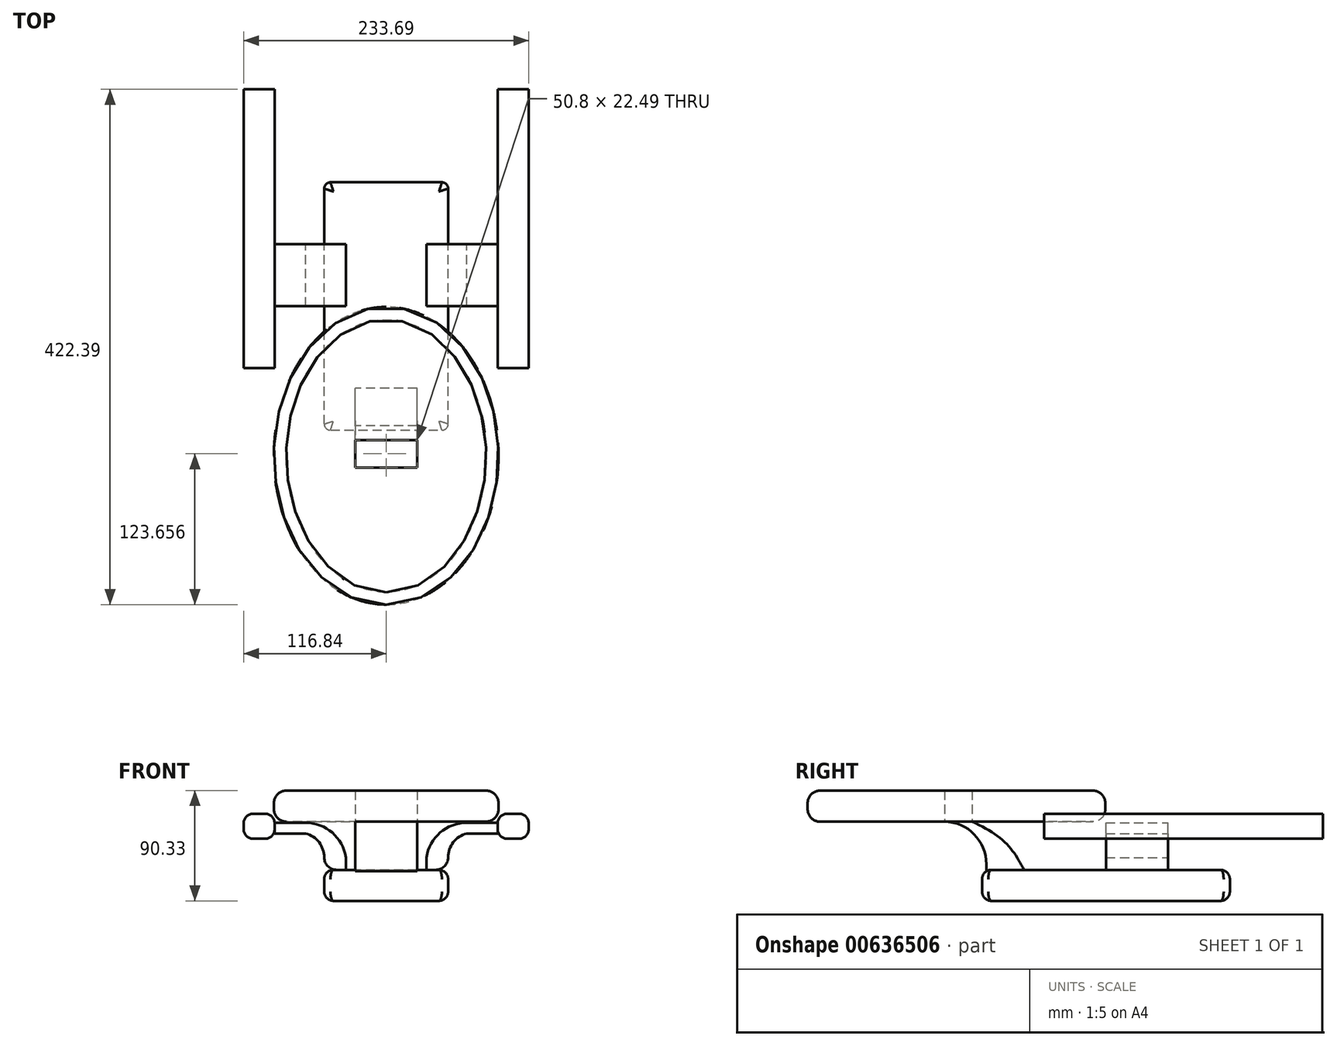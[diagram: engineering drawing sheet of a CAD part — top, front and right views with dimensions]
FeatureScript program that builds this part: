
annotation { "Feature Type Name" : "Feature", "Feature Type Description" : "" }
export const myFeature = defineFeature(function(context is Context, id is Id, definition is map)
    precondition{}
    {
        {
            var Q0;
            Q0=qCreatedBy(makeId("Front.planeOp"),FACE);
            var sketch = newSketch(context, id + "F0", { "sketchPlane" : qUnion([Q0])});
            skLineSegment(sketch, "E0.bottom", {"start": v(-50.8, 12.7) * mm, "end": v(50.8, 12.7) * mm});
            skLineSegment(sketch, "E0.top", {"start": v(-50.8, -12.7) * mm, "end": v(50.8, -12.7) * mm});
            skLineSegment(sketch, "E0.left", {"start": v(-50.8, 12.7) * mm, "end": v(-50.8, -12.7) * mm});
            skLineSegment(sketch, "E0.right", {"start": v(50.8, 12.7) * mm, "end": v(50.8, -12.7) * mm});
            skPoint(sketch, "E0.middle", {"position": v(0, 0) * mm});
            skLineSegment(sketch, "E1.bottom", {"start": v(-91.44, 38.28) * mm, "end": v(-116.84, 38.28) * mm});
            skLineSegment(sketch, "E1.top", {"start": v(-91.44, 58.6) * mm, "end": v(-116.84, 58.6) * mm});
            skLineSegment(sketch, "E1.left", {"start": v(-91.44, 38.28) * mm, "end": v(-91.44, 58.6) * mm});
            skLineSegment(sketch, "E1.right", {"start": v(-116.84, 38.28) * mm, "end": v(-116.84, 58.6) * mm});
            skPoint(sketch, "E1.middle", {"position": v(-104.14, 48.44) * mm});
            skLineSegment(sketch, "E2.bottom", {"start": v(91.45, 38.28) * mm, "end": v(116.85, 38.28) * mm});
            skLineSegment(sketch, "E2.top", {"start": v(91.45, 58.6) * mm, "end": v(116.85, 58.6) * mm});
            skLineSegment(sketch, "E2.left", {"start": v(91.45, 38.28) * mm, "end": v(91.45, 58.6) * mm});
            skLineSegment(sketch, "E2.right", {"start": v(116.85, 38.28) * mm, "end": v(116.85, 58.6) * mm});
            skPoint(sketch, "E2.middle", {"position": v(104.15, 48.44) * mm});
            skPoint(sketch, "E2.middle.positionSnap0", {"position": v(-91.44, 48.44) * mm});
            skPoint(sketch, "E2.centerSnap0", {"position": v(-91.44, 48.44) * mm});
            skLineSegment(sketch, "E3", {"start": v(50.8, 12.7) * mm, "end": v(50.8, 22.86) * mm});
            skLineSegment(sketch, "E4", {"start": v(-50.8, 12.7) * mm, "end": v(-50.8, 22.86) * mm});
            skArc(sketch, "E5", {"start": v(50.8, 22.86) * mm, "mid": v(55.06, 35.3) * mm, "end": v(66.05, 42.5) * mm});
            skLineSegment(sketch, "E6", {"start": v(66.05, 42.5) * mm, "end": v(91.45, 42.5) * mm});
            skArc(sketch, "E7", {"start": v(-50.8, 22.86) * mm, "mid": v(-55.06, 35.29) * mm, "end": v(-66.04, 42.5) * mm});
            skLineSegment(sketch, "E8", {"start": v(-66.04, 42.5) * mm, "end": v(-91.44, 42.38) * mm});
            skLineSegment(sketch, "E9", {"start": v(91.45, 51.35) * mm, "end": v(66.05, 51.35) * mm});
            skArc(sketch, "E10", {"start": v(66.05, 51.35) * mm, "mid": v(44.24, 43.24) * mm, "end": v(33.02, 22.86) * mm});
            skLineSegment(sketch, "E11", {"start": v(33.02, 22.86) * mm, "end": v(33.02, 12.7) * mm});
            skLineSegment(sketch, "E12", {"start": v(-91.44, 51.35) * mm, "end": v(-66.04, 51.35) * mm});
            skArc(sketch, "E13", {"start": v(-66.04, 51.35) * mm, "mid": v(-44.23, 43.24) * mm, "end": v(-33.02, 22.86) * mm});
            skLineSegment(sketch, "E14", {"start": v(-33.02, 22.86) * mm, "end": v(-33.02, 12.7) * mm});
            skSolve(sketch);
        }
        {
            var Q0;
            Q0=makeQuery(id+"F0.imprint","IMPRINT",FACE,{"disambiguationData":[TD([[makeQuery(id+"F0.imprint","IMPRINT",EDGE,{"derivedFrom":sQuery(id+"F0.wireOp",EDGE,"E0.top")}),1.0]])]});
            extrude(context, id + "F1", {"entities" : qUnion([Q0]), "depth" : 127 * mm, "offsetDistance" : 25.4 * mm, "hasSecondDirection" : true, "secondDirectionOppositeDirection" : true, "secondDirectionDepth" : 76.2 * mm});
        }
        {
            var Q0;
            {var subQ3=sQuery(id+"F0.wireOp",EDGE,"E2.bottom");Q0=makeQuery(id+"F0.imprint","IMPRINT",FACE,{"disambiguationData":[TD([[makeQuery(id+"F0.imprint","IMPRINT",EDGE,{"derivedFrom":subQ3}),1.0]])]});}
            extrude(context, id + "F2", {"entities" : qUnion([Q0]), "depth" : 76.2 * mm, "offsetDistance" : 25.4 * mm, "hasSecondDirection" : true, "secondDirectionOppositeDirection" : true, "secondDirectionDepth" : 152.4 * mm});
        }
        {
            var Q0;
            {var subQ3=sQuery(id+"F0.wireOp",EDGE,"E1.bottom");Q0=makeQuery(id+"F0.imprint","IMPRINT",FACE,{"disambiguationData":[TD([[makeQuery(id+"F0.imprint","IMPRINT",EDGE,{"derivedFrom":subQ3}),-1.0]])]});}
            extrude(context, id + "F3", {"entities" : qUnion([Q0]), "depth" : 76.2 * mm, "offsetDistance" : 25.4 * mm, "hasSecondDirection" : true, "secondDirectionOppositeDirection" : true, "secondDirectionDepth" : 152.4 * mm});
        }
        {
            var Q0;
            {var subQ0=sQuery(id+"F0.wireOp",EDGE,"E4");Q0=makeQuery(id+"F0.imprint","IMPRINT",FACE,{"disambiguationData":[TD([[makeQuery(id+"F0.imprint","IMPRINT",EDGE,{"derivedFrom":subQ0}),-1.0]])]});}
            extrude(context, id + "F4", {"entities" : qUnion([Q0]), "depth" : 25.4 * mm, "offsetDistance" : 25.4 * mm, "hasSecondDirection" : true, "secondDirectionOppositeDirection" : true, "secondDirectionDepth" : 25.4 * mm});
        }
        {
            var Q0;
            {var subQ0=sQuery(id+"F0.wireOp",EDGE,"E3");Q0=makeQuery(id+"F0.imprint","IMPRINT",FACE,{"disambiguationData":[TD([[makeQuery(id+"F0.imprint","IMPRINT",EDGE,{"derivedFrom":subQ0}),1.0]])]});}
            extrude(context, id + "F5", {"entities" : qUnion([Q0]), "depth" : 25.4 * mm, "offsetDistance" : 25.4 * mm, "hasSecondDirection" : true, "secondDirectionOppositeDirection" : true, "secondDirectionDepth" : 25.4 * mm});
        }
        {
            var Q0;
            Q0=qCreatedBy(makeId("Right.planeOp"),FACE);
            var sketch = newSketch(context, id + "F6", { "sketchPlane" : qUnion([Q0])});
            skLineSegment(sketch, "E15", {"start": v(-123.49, 12.39) * mm, "end": v(-123.49, 17.47) * mm});
            skArc(sketch, "E16", {"start": v(-123.49, 17.47) * mm, "mid": v(-133.92, 42.3) * mm, "end": v(-158.95, 52.23) * mm});
            skLineSegment(sketch, "E17", {"start": v(-158.95, 52.23) * mm, "end": v(-158.95, 62.4) * mm});
            skFitSpline(sketch, "E18", {"points": [v(-158.95, 62.4) * mm, v(-110.55, 37.49) * mm, v(-92.4, 12.39) * mm], "startDerivative": vector(97.08, -39.51) * mm, "endDerivative": vector(33.03, -61.53) * mm});
            skLineSegment(sketch, "E19", {"start": v(-123.49, 12.39) * mm, "end": v(-92.4, 12.39) * mm});
            skLineSegment(sketch, "E20.bottom", {"start": v(-240.74, 52.23) * mm, "end": v(-77.16, 52.23) * mm});
            skLineSegment(sketch, "E20.top", {"start": v(-240.74, 72.55) * mm, "end": v(-77.16, 72.55) * mm});
            skLineSegment(sketch, "E20.left", {"start": v(-240.74, 52.23) * mm, "end": v(-240.74, 72.55) * mm});
            skLineSegment(sketch, "E20.right", {"start": v(-77.16, 52.23) * mm, "end": v(-77.16, 72.55) * mm});
            skSolve(sketch);
        }
        {
            var Q0;
            {var subQ2=sQuery(id+"F6.wireOp",EDGE,"E15");Q0=makeQuery(id+"F6.imprint","IMPRINT",FACE,{"disambiguationData":[TD([[makeQuery(id+"F6.imprint","IMPRINT",EDGE,{"derivedFrom":subQ2}),-1.0]])]});}
            extrude(context, id + "F7", {"entities" : qUnion([Q0]), "operationType" : NewBodyOperationType.ADD, "endBound" : BoundingType.SYMMETRIC, "depth" : 50.8 * mm, "offsetDistance" : 25.4 * mm});
        }
        {
            var Q0;
            Q0=makeQuery(id+"F7.opExtrude","SWEPT_FACE",FACE,{"disambiguationData":[OSD([sQuery(id+"F6.wireOp",EDGE,"E20.bottom")])]});
            var sketch = newSketch(context, id + "F8", { "sketchPlane" : qUnion([Q0])});
            skEllipse(sketch, "E21", {"center": v(0, -147.96) * mm, "majorRadius": 122.03 * mm, "minorRadius": 92.08 * mm, "majorAxis": v(0, -1)});
            skPoint(sketch, "E21.centerSnap0", {"position": v(0, -157.58) * mm});
            skSolve(sketch);
        }
        {
            var Q0;
            Q0=makeQuery(id+"F8.imprint","IMPRINT",FACE,{"disambiguationData":[TD([[makeQuery(id+"F8.imprint","IMPRINT",EDGE,{"derivedFrom":sQuery(id+"F8.wireOp",EDGE,"E21")}),1.0]])]});
            extrude(context, id + "F9", {"entities" : qUnion([Q0]), "depth" : 25.4 * mm, "offsetDistance" : 25.4 * mm});
        }
        {
            var Q0;
            Q0=makeQuery(id+"F1.opExtrude","CAP_EDGE",EDGE,{"disambiguationData":[OSD([sQuery(id+"F0.wireOp",EDGE,"E0.right")])],"isStart":false});
            var Q1;
            Q1=makeQuery(id+"F1.opExtrude","CAP_EDGE",EDGE,{"disambiguationData":[OSD([sQuery(id+"F0.wireOp",EDGE,"E0.left")])],"isStart":false});
            var Q2;
            Q2=makeQuery(id+"F1.opExtrude","CAP_EDGE",EDGE,{"disambiguationData":[OSD([sQuery(id+"F0.wireOp",EDGE,"E0.right")])],"isStart":true});
            var Q3;
            Q3=makeQuery(id+"F1.opExtrude","CAP_EDGE",EDGE,{"disambiguationData":[OSD([sQuery(id+"F0.wireOp",EDGE,"E0.left")])],"isStart":true});
            fillet(context, id + "F10", {"entities" : qUnion([Q0, Q1, Q2, Q3]), "radius" : 5.08 * mm, "tangentPropagation" : true, "allowEdgeOverflow" : false});
        }
        {
            var Q0;
            Q0=makeQuery(id+"F1.opExtrude","SWEPT_EDGE",EDGE,{"disambiguationData":[OSD([sQuery(id+"F0.wireOp",EDGE,"E0.bottom"),sQuery(id+"F0.wireOp",EDGE,"E0.right"),sQuery(id+"F0.wireOp",EDGE,"E3")])]});
            var Q1;
            Q1=makeQuery(id+"F1.opExtrude","SWEPT_EDGE",EDGE,{"disambiguationData":[OSD([sQuery(id+"F0.wireOp",EDGE,"E0.top"),sQuery(id+"F0.wireOp",EDGE,"E0.right")])]});
            var Q2;
            Q2=makeQuery(id+"F1.opExtrude","SWEPT_EDGE",EDGE,{"disambiguationData":[OSD([sQuery(id+"F0.wireOp",EDGE,"E0.top"),sQuery(id+"F0.wireOp",EDGE,"E0.left")])]});
            var Q3;
            Q3=makeQuery(id+"F1.opExtrude","SWEPT_EDGE",EDGE,{"disambiguationData":[OSD([sQuery(id+"F0.wireOp",EDGE,"E0.bottom"),sQuery(id+"F0.wireOp",EDGE,"E0.left"),sQuery(id+"F0.wireOp",EDGE,"E4")])]});
            fillet(context, id + "F11", {"entities" : qUnion([Q0, Q1, Q2, Q3]), "radius" : 7.62 * mm, "tangentPropagation" : true, "allowEdgeOverflow" : false});
        }
        {
            var Q0;
            Q0=makeQuery(id+"F9.opExtrude","CAP_EDGE",EDGE,{"disambiguationData":[OSD([sQuery(id+"F8.wireOp",EDGE,"E21")])],"isStart":true});
            var Q1;
            Q1=makeQuery(id+"F9.opExtrude","CAP_EDGE",EDGE,{"disambiguationData":[OSD([sQuery(id+"F8.wireOp",EDGE,"E21")])],"isStart":false});
            fillet(context, id + "F12", {"entities" : qUnion([Q0, Q1]), "radius" : 10.16 * mm, "tangentPropagation" : true, "allowEdgeOverflow" : false});
        }
        {
            var Q0;
            Q0=makeQuery(id+"F2.opExtrude","SWEPT_EDGE",EDGE,{"disambiguationData":[OSD([sQuery(id+"F0.wireOp",EDGE,"E2.top"),sQuery(id+"F0.wireOp",EDGE,"E2.right")])]});
            var Q1;
            Q1=makeQuery(id+"F2.opExtrude","SWEPT_EDGE",EDGE,{"disambiguationData":[OSD([sQuery(id+"F0.wireOp",EDGE,"E2.top"),sQuery(id+"F0.wireOp",EDGE,"E2.left")])]});
            var Q2;
            Q2=makeQuery(id+"F2.opExtrude","SWEPT_EDGE",EDGE,{"disambiguationData":[OSD([sQuery(id+"F0.wireOp",EDGE,"E2.bottom"),sQuery(id+"F0.wireOp",EDGE,"E2.left")])]});
            var Q3;
            Q3=makeQuery(id+"F3.opExtrude","SWEPT_EDGE",EDGE,{"disambiguationData":[OSD([sQuery(id+"F0.wireOp",EDGE,"E1.top"),sQuery(id+"F0.wireOp",EDGE,"E1.left")])]});
            var Q4;
            Q4=makeQuery(id+"F3.opExtrude","SWEPT_EDGE",EDGE,{"disambiguationData":[OSD([sQuery(id+"F0.wireOp",EDGE,"E1.top"),sQuery(id+"F0.wireOp",EDGE,"E1.right")])]});
            var Q5;
            Q5=makeQuery(id+"F3.opExtrude","SWEPT_EDGE",EDGE,{"disambiguationData":[OSD([sQuery(id+"F0.wireOp",EDGE,"E1.bottom"),sQuery(id+"F0.wireOp",EDGE,"E1.right")])]});
            var Q6;
            Q6=makeQuery(id+"F3.opExtrude","SWEPT_EDGE",EDGE,{"disambiguationData":[OSD([sQuery(id+"F0.wireOp",EDGE,"E1.bottom"),sQuery(id+"F0.wireOp",EDGE,"E1.left")])]});
            var Q7;
            Q7=makeQuery(id+"F2.opExtrude","SWEPT_EDGE",EDGE,{"disambiguationData":[OSD([sQuery(id+"F0.wireOp",EDGE,"E2.bottom"),sQuery(id+"F0.wireOp",EDGE,"E2.right")])]});
            fillet(context, id + "F13", {"entities" : qUnion([Q0, Q1, Q2, Q3, Q4, Q5, Q6, Q7]), "radius" : 7.62 * mm, "tangentPropagation" : true, "allowEdgeOverflow" : false});
        }
        {
            var Q0;
            Q0=makeQuery(id+"F5.opExtrude","SWEPT_EDGE",EDGE,{"disambiguationData":[OSD([sQuery(id+"F0.wireOp",EDGE,"E0.bottom"),sQuery(id+"F0.wireOp",EDGE,"E0.right"),sQuery(id+"F0.wireOp",EDGE,"E3")])]});
            var Q1;
            Q1=makeQuery(id+"F4.opExtrude","SWEPT_EDGE",EDGE,{"disambiguationData":[OSD([sQuery(id+"F0.wireOp",EDGE,"E0.bottom"),sQuery(id+"F0.wireOp",EDGE,"E0.left"),sQuery(id+"F0.wireOp",EDGE,"E4")])]});
            fillet(context, id + "F14", {"entities" : qUnion([Q0, Q1]), "radius" : 10.16 * mm, "tangentPropagation" : true, "allowEdgeOverflow" : false});
        }
    });
